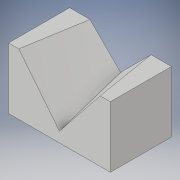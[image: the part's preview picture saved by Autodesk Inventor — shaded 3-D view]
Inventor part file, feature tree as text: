
AUTODESK INVENTOR PART (.ipt)
format: ipt  version: 2018 (Build 220112000, 112)  size: 116,736 bytes
history: native  units: in
note: dims shown in document units (in); Inventor stores cm internally (conversion verified against a paired STEP export)
features: sketch x3, extrude x1, loft x1
ambient origin geometry x8: Origin, YZ Plane, XZ Plane, XY Plane, X Axis, Y Axis, Z Axis, Center Point
bodies: Solid1 (feature_tree)
feature tree (5):
  extrude  "Extrusion1"  Depth=1.5in
  loft  "Loft1"
  sketch  "Sketch1"  dims[d0=2.5in d1=1.5in]
  sketch  "Sketch2"  dims[d2=1.5in d3=0.0in d4=0.25in]
  sketch  "Sketch4"  dims[d5=0.25in d6=0.25in d8=0.75in d9=0.5in d10=0.5in d11=0.0in d12=90.0deg d13=0.0in d14=90.0deg]
